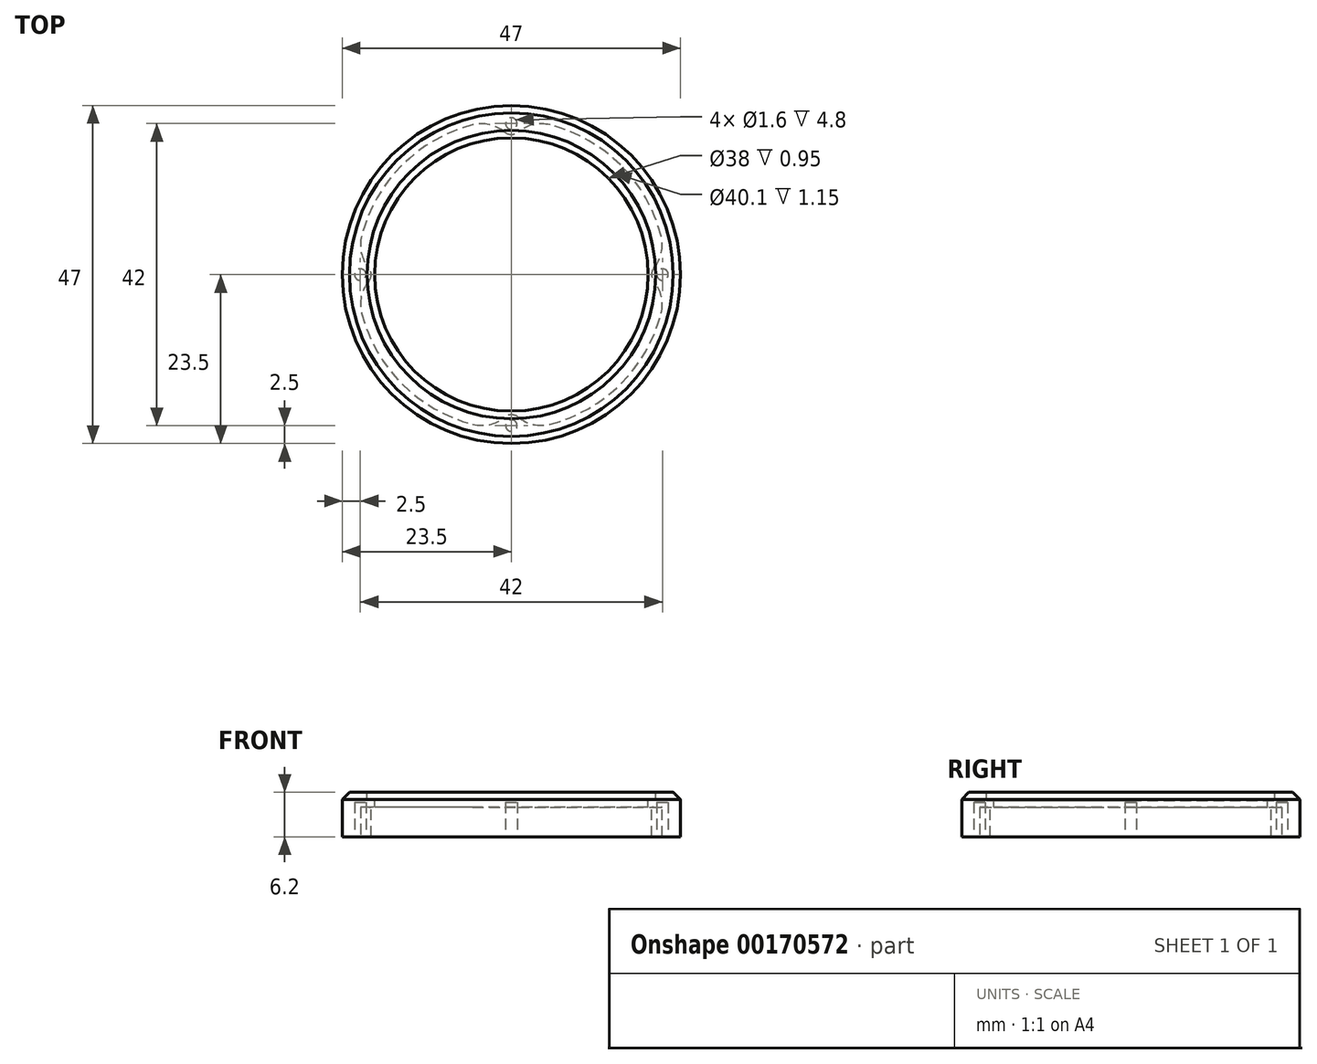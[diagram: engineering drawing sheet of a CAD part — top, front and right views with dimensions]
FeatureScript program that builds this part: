
annotation { "Feature Type Name" : "Feature", "Feature Type Description" : "" }
export const myFeature = defineFeature(function(context is Context, id is Id, definition is map)
    precondition{}
    {
        {
            var Q0;
            Q0=qCreatedBy(makeId("Top.planeOp"),FACE);
            var sketch = newSketch(context, id + "F0", { "sketchPlane" : qUnion([Q0])});
            skCircle(sketch, "E0", {"center": v(0, 0) * mm, "radius": 23.5 * mm});
            skSolve(sketch);
        }
        {
            var Q0;
            Q0 = qSketchRegion(id + "F0", true);
            extrude(context, id + "F1", {"entities" : qUnion([Q0]), "depth" : 6.2 * mm});
        }
        {
            var Q0;
            Q0=makeQuery(id+"F1.opExtrude","CAP_FACE",FACE,{"disambiguationData":[OSD([sQuery(id+"F0.wireOp",EDGE,"E0")])],"isStart":true});
            shell(context, id + "F2", {"entities" : qUnion([Q0]), "thickness" : 2 * mm});
        }
        {
            var Q0;
            Q0=makeQuery(id+"F1.opExtrude","CAP_EDGE",EDGE,{"disambiguationData":[OSD([sQuery(id+"F0.wireOp",EDGE,"E0")])],"isStart":false});
            chamfer(context, id + "F3", {"entities" : qUnion([Q0]), "width" : 1 * mm, "tangentPropagation" : true});
        }
        {
            var Q0;
            Q0=makeQuery(id+"F1.opExtrude","CAP_FACE",FACE,{"disambiguationData":[OSD([sQuery(id+"F0.wireOp",EDGE,"E0")])],"isStart":false});
            var sketch = newSketch(context, id + "F4", { "sketchPlane" : qUnion([Q0])});
            skCircle(sketch, "E1", {"center": v(0, 0) * mm, "radius": 19 * mm});
            skSolve(sketch);
        }
        {
            var Q0;
            Q0 = qSketchRegion(id + "F4", true);
            extrude(context, id + "F5", {"entities" : qUnion([Q0]), "operationType" : NewBodyOperationType.REMOVE, "endBound" : BoundingType.THROUGH_ALL, "oppositeDirection" : true, "depth" : 25 * mm});
        }
        {
            var Q0;
            Q0=makeQuery(id+"F1.opExtrude","CAP_FACE",FACE,{"disambiguationData":[OSD([sQuery(id+"F0.wireOp",EDGE,"E0")])],"isStart":false});
            var sketch = newSketch(context, id + "F6", { "sketchPlane" : qUnion([Q0])});
            skCircle(sketch, "E2", {"center": v(0, 0) * mm, "radius": 20.05 * mm});
            skSolve(sketch);
        }
        {
            var Q0;
            Q0 = qSketchRegion(id + "F6", true);
            extrude(context, id + "F7", {"entities" : qUnion([Q0]), "operationType" : NewBodyOperationType.REMOVE, "oppositeDirection" : true, "depth" : 1.15 * mm});
        }
        {
            var Q0;
            {var subQ0=sQuery(id+"F0.wireOp",EDGE,"E0");Q0=makeQuery(id+"F2.opShell","OFFSET_FACE",FACE,{"disambiguationData":[OSD([subQ0]),TDD([makeQuery(id+"F1.opExtrude","CAP_FACE",FACE,{"disambiguationData":[OSD([subQ0])],"isStart":false})])]});}
            extrude(context, id + "F8", {"entities" : qUnion([Q0]), "operationType" : NewBodyOperationType.ADD, "depth" : 0.1 * mm});
        }
        {
            var Q0;
            Q0=makeQuery(id+"F8.opExtrude","CAP_FACE",FACE,{"disambiguationData":[OSD([sQuery(id+"F0.wireOp",EDGE,"E0")])],"isStart":false});
            var sketch = newSketch(context, id + "F9", { "sketchPlane" : qUnion([Q0])});
            skCircle(sketch, "E3", {"center": v(0, 21) * mm, "radius": 1.5 * mm});
            skCircle(sketch, "E4.1.0", {"center": v(-21, 0) * mm, "radius": 1.5 * mm});
            skCircle(sketch, "E4.2.0", {"center": v(0, -21) * mm, "radius": 1.5 * mm});
            skCircle(sketch, "E4.3.0", {"center": v(21, 0) * mm, "radius": 1.5 * mm});
            skPoint(sketch, "E4.center", {"position": v(0, 0) * mm});
            skSolve(sketch);
        }
        {
            var Q0;
            Q0 = qSketchRegion(id + "F9", true);
            var Q1;
            Q1=makeQuery(id+"F1.opExtrude","CAP_FACE",FACE,{"disambiguationData":[OSD([sQuery(id+"F0.wireOp",EDGE,"E0")])],"isStart":true});
            extrude(context, id + "F10", {"entities" : qUnion([Q0]), "operationType" : NewBodyOperationType.ADD, "endBound" : BoundingType.UP_TO_SURFACE, "endBoundEntityFace" : qUnion([Q1]), "depth" : 25 * mm});
        }
        {
            var Q0;
            {var subQ0=sQuery(id+"F0.wireOp",EDGE,"E0");Q0=makeQuery(id+"F10.boolean.opBoolean","INTERSECT",EDGE,{"disambiguationData":[OD(0.0)],"derivedFrom":[makeQuery(id+"F2.opShell","OFFSET_FACE",FACE,{"disambiguationData":[OSD([subQ0]),TDD([makeQuery(id+"F1.opExtrude","SWEPT_FACE",FACE,{"disambiguationData":[OSD([subQ0])]})])]}),makeQuery(id+"F10.opExtrude","SWEPT_FACE",FACE,{"disambiguationData":[OSD([sQuery(id+"F9.wireOp",EDGE,"E4.3.0")])]})]});}
            var Q1;
            {var subQ0=sQuery(id+"F0.wireOp",EDGE,"E0");Q1=makeQuery(id+"F10.boolean.opBoolean","INTERSECT",EDGE,{"disambiguationData":[OD(1.0)],"derivedFrom":[makeQuery(id+"F2.opShell","OFFSET_FACE",FACE,{"disambiguationData":[OSD([subQ0]),TDD([makeQuery(id+"F1.opExtrude","SWEPT_FACE",FACE,{"disambiguationData":[OSD([subQ0])]})])]}),makeQuery(id+"F10.opExtrude","SWEPT_FACE",FACE,{"disambiguationData":[OSD([sQuery(id+"F9.wireOp",EDGE,"E3")])]})]});}
            var Q2;
            {var subQ0=sQuery(id+"F0.wireOp",EDGE,"E0");Q2=makeQuery(id+"F10.boolean.opBoolean","INTERSECT",EDGE,{"disambiguationData":[OD(0.0)],"derivedFrom":[makeQuery(id+"F2.opShell","OFFSET_FACE",FACE,{"disambiguationData":[OSD([subQ0]),TDD([makeQuery(id+"F1.opExtrude","SWEPT_FACE",FACE,{"disambiguationData":[OSD([subQ0])]})])]}),makeQuery(id+"F10.opExtrude","SWEPT_FACE",FACE,{"disambiguationData":[OSD([sQuery(id+"F9.wireOp",EDGE,"E3")])]})]});}
            var Q3;
            {var subQ0=sQuery(id+"F0.wireOp",EDGE,"E0");Q3=makeQuery(id+"F10.boolean.opBoolean","INTERSECT",EDGE,{"disambiguationData":[OD(0.0)],"derivedFrom":[makeQuery(id+"F2.opShell","OFFSET_FACE",FACE,{"disambiguationData":[OSD([subQ0]),TDD([makeQuery(id+"F1.opExtrude","SWEPT_FACE",FACE,{"disambiguationData":[OSD([subQ0])]})])]}),makeQuery(id+"F10.opExtrude","SWEPT_FACE",FACE,{"disambiguationData":[OSD([sQuery(id+"F9.wireOp",EDGE,"E4.1.0")])]})]});}
            var Q4;
            {var subQ0=sQuery(id+"F0.wireOp",EDGE,"E0");Q4=makeQuery(id+"F10.boolean.opBoolean","INTERSECT",EDGE,{"disambiguationData":[OD(1.0)],"derivedFrom":[makeQuery(id+"F2.opShell","OFFSET_FACE",FACE,{"disambiguationData":[OSD([subQ0]),TDD([makeQuery(id+"F1.opExtrude","SWEPT_FACE",FACE,{"disambiguationData":[OSD([subQ0])]})])]}),makeQuery(id+"F10.opExtrude","SWEPT_FACE",FACE,{"disambiguationData":[OSD([sQuery(id+"F9.wireOp",EDGE,"E4.1.0")])]})]});}
            var Q5;
            {var subQ0=sQuery(id+"F0.wireOp",EDGE,"E0");Q5=makeQuery(id+"F10.boolean.opBoolean","INTERSECT",EDGE,{"disambiguationData":[OD(0.0)],"derivedFrom":[makeQuery(id+"F2.opShell","OFFSET_FACE",FACE,{"disambiguationData":[OSD([subQ0]),TDD([makeQuery(id+"F1.opExtrude","SWEPT_FACE",FACE,{"disambiguationData":[OSD([subQ0])]})])]}),makeQuery(id+"F10.opExtrude","SWEPT_FACE",FACE,{"disambiguationData":[OSD([sQuery(id+"F9.wireOp",EDGE,"E4.2.0")])]})]});}
            var Q6;
            {var subQ0=sQuery(id+"F0.wireOp",EDGE,"E0");Q6=makeQuery(id+"F10.boolean.opBoolean","INTERSECT",EDGE,{"disambiguationData":[OD(1.0)],"derivedFrom":[makeQuery(id+"F2.opShell","OFFSET_FACE",FACE,{"disambiguationData":[OSD([subQ0]),TDD([makeQuery(id+"F1.opExtrude","SWEPT_FACE",FACE,{"disambiguationData":[OSD([subQ0])]})])]}),makeQuery(id+"F10.opExtrude","SWEPT_FACE",FACE,{"disambiguationData":[OSD([sQuery(id+"F9.wireOp",EDGE,"E4.2.0")])]})]});}
            var Q7;
            {var subQ0=sQuery(id+"F0.wireOp",EDGE,"E0");Q7=makeQuery(id+"F10.boolean.opBoolean","INTERSECT",EDGE,{"disambiguationData":[OD(1.0)],"derivedFrom":[makeQuery(id+"F2.opShell","OFFSET_FACE",FACE,{"disambiguationData":[OSD([subQ0]),TDD([makeQuery(id+"F1.opExtrude","SWEPT_FACE",FACE,{"disambiguationData":[OSD([subQ0])]})])]}),makeQuery(id+"F10.opExtrude","SWEPT_FACE",FACE,{"disambiguationData":[OSD([sQuery(id+"F9.wireOp",EDGE,"E4.3.0")])]})]});}
            fillet(context, id + "F11", {"entities" : qUnion([Q0, Q1, Q2, Q3, Q4, Q5, Q6, Q7]), "radius" : 5 * mm, "tangentPropagation" : true, "allowEdgeOverflow" : false});
        }
        {
            var Q0;
            {var subQ0=sQuery(id+"F0.wireOp",EDGE,"E0");Q0=makeQuery(id+"F10.boolean.opBoolean","MERGE",FACE,{"derivedFrom":[makeQuery(id+"F1.opExtrude","CAP_FACE",FACE,{"disambiguationData":[OSD([subQ0])],"isStart":true}),makeQuery(id+"F10.opExtrude","CAP_FACE",FACE,{"disambiguationData":[OSD([subQ0]),ownerDisambiguation([makeQuery(id+"F10.opExtrude","SWEPT_BODY",BODY,{"disambiguationData":[OSD([sQuery(id+"F9.wireOp",EDGE,"E3")])]})])],"isStart":false}),makeQuery(id+"F10.opExtrude","CAP_FACE",FACE,{"disambiguationData":[OSD([subQ0]),ownerDisambiguation([makeQuery(id+"F10.opExtrude","SWEPT_BODY",BODY,{"disambiguationData":[OSD([sQuery(id+"F9.wireOp",EDGE,"E4.1.0")])]})])],"isStart":false}),makeQuery(id+"F10.opExtrude","CAP_FACE",FACE,{"disambiguationData":[OSD([subQ0]),ownerDisambiguation([makeQuery(id+"F10.opExtrude","SWEPT_BODY",BODY,{"disambiguationData":[OSD([sQuery(id+"F9.wireOp",EDGE,"E4.2.0")])]})])],"isStart":false}),makeQuery(id+"F10.opExtrude","CAP_FACE",FACE,{"disambiguationData":[OSD([subQ0]),ownerDisambiguation([makeQuery(id+"F10.opExtrude","SWEPT_BODY",BODY,{"disambiguationData":[OSD([sQuery(id+"F9.wireOp",EDGE,"E4.3.0")])]})])],"isStart":false})]});}
            var sketch = newSketch(context, id + "F12", { "sketchPlane" : qUnion([Q0])});
            skCircle(sketch, "E5", {"center": v(0, -21) * mm, "radius": 0.8 * mm});
            skCircle(sketch, "E6.1.0", {"center": v(21, 0) * mm, "radius": 0.8 * mm});
            skCircle(sketch, "E6.2.0", {"center": v(0, 21) * mm, "radius": 0.8 * mm});
            skCircle(sketch, "E6.3.0", {"center": v(-21, 0) * mm, "radius": 0.8 * mm});
            skPoint(sketch, "E6.center", {"position": v(0, 0) * mm});
            skSolve(sketch);
        }
        {
            var Q0;
            Q0 = qSketchRegion(id + "F12", true);
            extrude(context, id + "F13", {"entities" : qUnion([Q0]), "operationType" : NewBodyOperationType.REMOVE, "oppositeDirection" : true, "depth" : 4.8 * mm});
        }
    });
